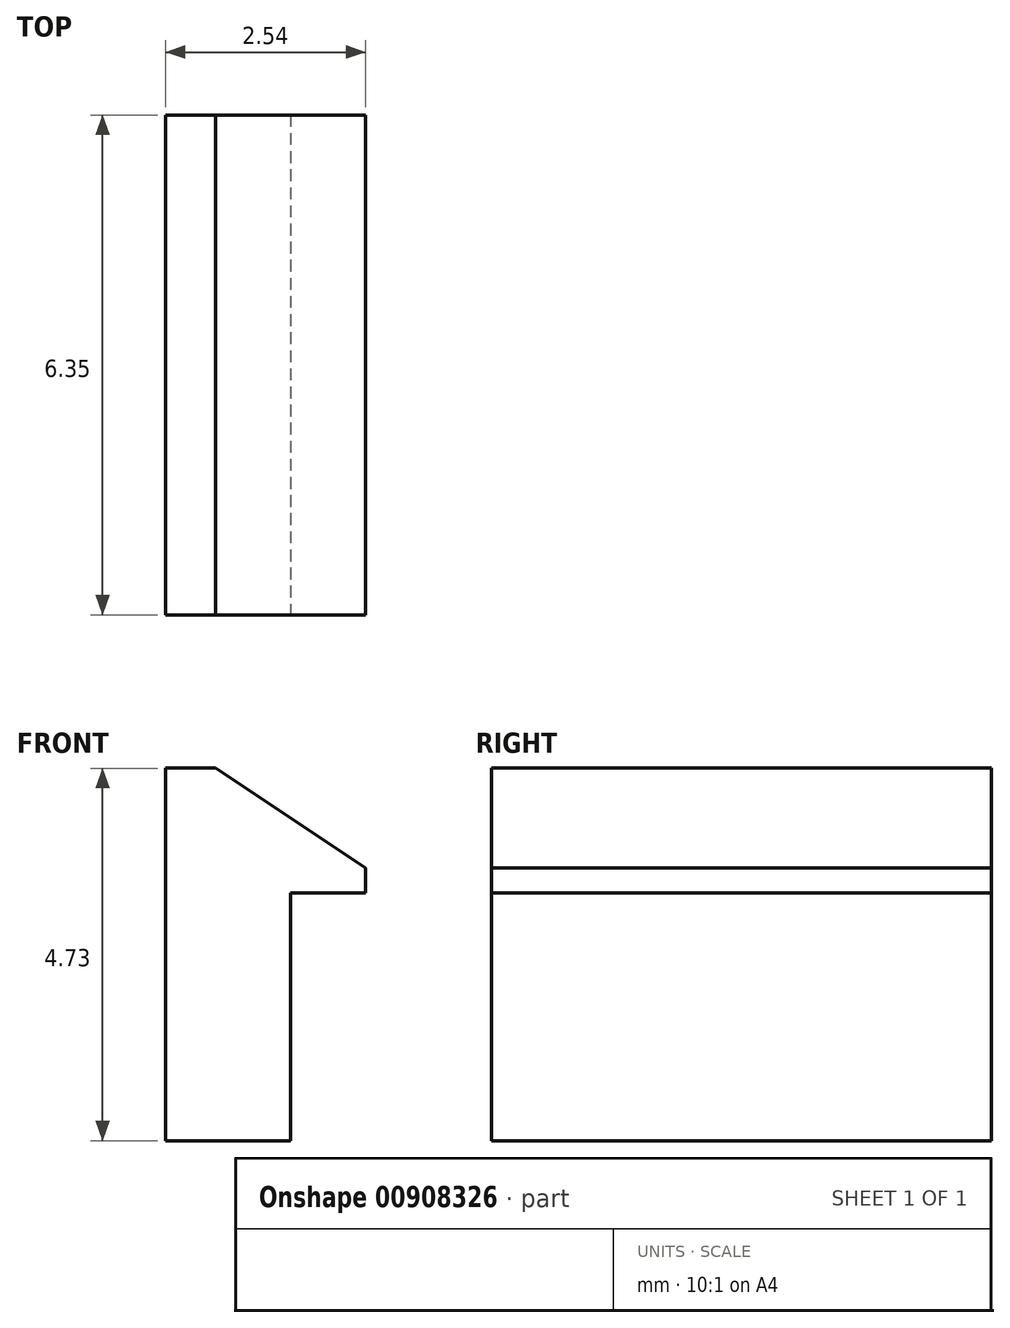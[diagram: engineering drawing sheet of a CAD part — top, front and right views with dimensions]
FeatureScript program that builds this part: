
annotation { "Feature Type Name" : "Feature", "Feature Type Description" : "" }
export const myFeature = defineFeature(function(context is Context, id is Id, definition is map)
    precondition{}
    {
        {
            var Q0;
            Q0=qCreatedBy(makeId("Right.planeOp"),FACE);
            var sketch = newSketch(context, id + "F0", { "sketchPlane" : qUnion([Q0])});
            skLineSegment(sketch, "E0.bottom", {"start": v(0, 0) * mm, "end": v(6.35, 0) * mm});
            skLineSegment(sketch, "E0.top", {"start": v(0, 3.18) * mm, "end": v(6.35, 3.18) * mm});
            skLineSegment(sketch, "E0.left", {"start": v(0, 0) * mm, "end": v(0, 3.18) * mm});
            skLineSegment(sketch, "E0.right", {"start": v(6.35, 0) * mm, "end": v(6.35, 3.17) * mm});
            skSolve(sketch);
        }
        {
            var Q0;
            Q0=makeQuery(id+"F0.imprint","IMPRINT",FACE,{"disambiguationData":[TD([[makeQuery(id+"F0.imprint","IMPRINT",EDGE,{"derivedFrom":sQuery(id+"F0.wireOp",EDGE,"E0.bottom")}),1.0]])]});
            extrude(context, id + "F1", {"entities" : qUnion([Q0]), "depth" : 1.59 * mm, "offsetDistance" : 25.4 * mm});
        }
        {
            var Q0;
            Q0=qCreatedBy(makeId("Right.planeOp"),FACE);
            var sketch = newSketch(context, id + "F2", { "sketchPlane" : qUnion([Q0])});
            skLineSegment(sketch, "E1.bottom", {"start": v(0, 3.15) * mm, "end": v(6.35, 3.15) * mm});
            skLineSegment(sketch, "E1.top", {"start": v(0, 4.73) * mm, "end": v(6.35, 4.73) * mm});
            skLineSegment(sketch, "E1.left", {"start": v(0, 3.15) * mm, "end": v(0, 4.73) * mm});
            skLineSegment(sketch, "E1.right", {"start": v(6.35, 3.15) * mm, "end": v(6.35, 4.73) * mm});
            skSolve(sketch);
        }
        {
            var Q0;
            Q0=makeQuery(id+"F2.imprint","IMPRINT",FACE,{"disambiguationData":[TD([[makeQuery(id+"F2.imprint","IMPRINT",EDGE,{"derivedFrom":sQuery(id+"F2.wireOp",EDGE,"E1.bottom")}),1.0]])]});
            extrude(context, id + "F3", {"entities" : qUnion([Q0]), "operationType" : NewBodyOperationType.ADD, "depth" : 2.54 * mm, "offsetDistance" : 25.4 * mm});
        }
        {
            var Q0;
            Q0=makeQuery(id+"F3.opExtrude","CAP_EDGE",EDGE,{"disambiguationData":[OSD([sQuery(id+"F2.wireOp",EDGE,"E1.top")])],"isStart":false});
            chamfer(context, id + "F4", {"entities" : qUnion([Q0]), "chamferType" : ChamferType.TWO_OFFSETS, "width1" : 1.9 * mm, "oppositeDirection" : false, "width2" : 1.27 * mm, "tangentPropagation" : true});
        }
    });
